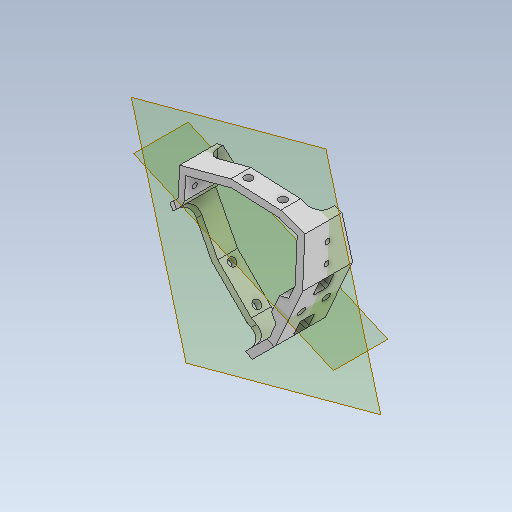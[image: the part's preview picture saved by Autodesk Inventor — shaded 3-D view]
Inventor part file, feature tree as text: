
AUTODESK INVENTOR PART (.ipt)
format: ipt  version: 2023 (Build 270158000, 158)  size: 300,032 bytes
history: native  units: mm
features: sketch x15, plane x4, other x3
ambient origin geometry x8: Origin, YZ Plane, XZ Plane, XY Plane, X Axis, Y Axis, Z Axis, Center Point
bodies: Solid1 (feature_tree)
feature tree (22):
  other  "leg_holder_2.ipt"
  other  "Solid2::leg_holder_2.ipt"
  other  "TaggingFeature1"
  sketch  "Sketch1"  dims[d0=10.0mm]
  sketch  "Sketch4"
  sketch  "Sketch5"
  sketch  "Sketch6"
  sketch  "Sketch7"
  sketch  "Sketch8"
  sketch  "Sketch10"
  sketch  "Sketch11"
  sketch  "Sketch12"
  sketch  "Sketch13"
  sketch  "Sketch14"
  sketch  "Sketch15"
  sketch  "Sketch18"
  sketch  "Sketch19"
  sketch  "Sketch20"
  plane  "Work Plane1"
  plane  "Work Plane2"
  plane  "Work Plane3"
  plane  "Work Plane4"
